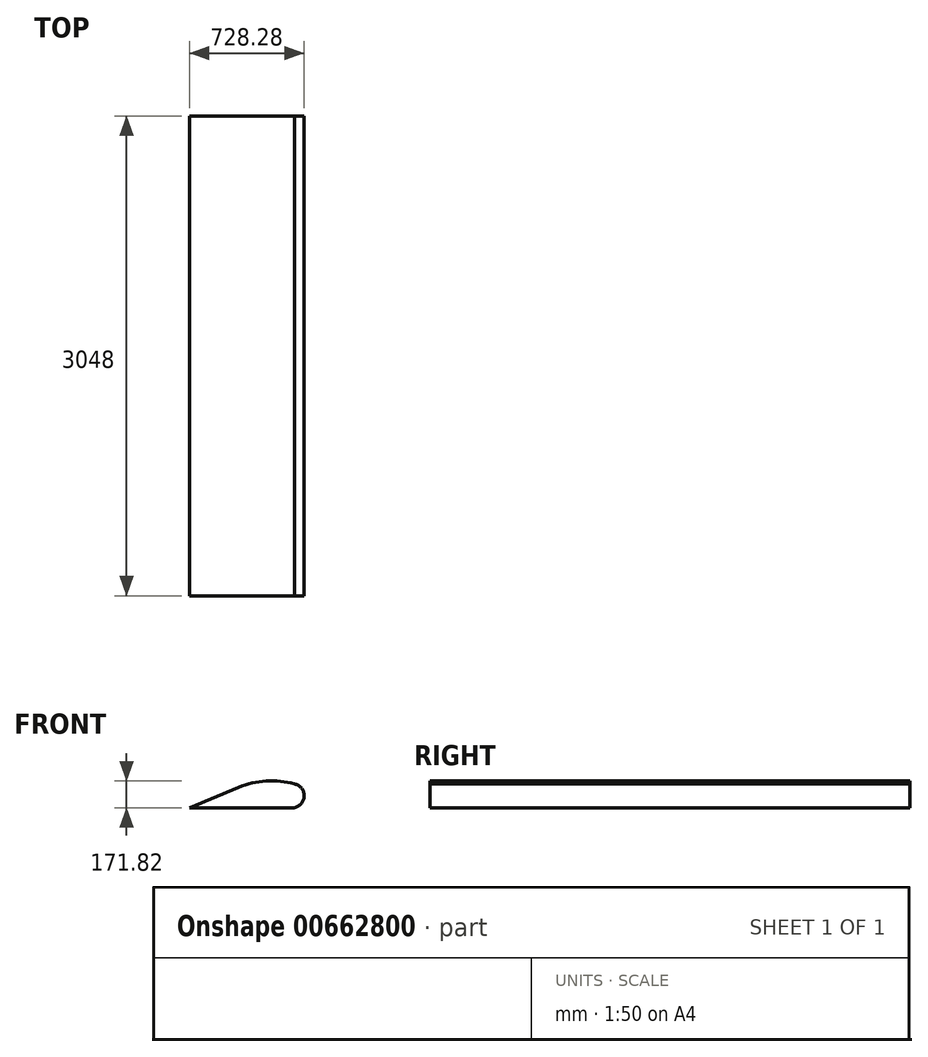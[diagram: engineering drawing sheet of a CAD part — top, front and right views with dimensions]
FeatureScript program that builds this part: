
annotation { "Feature Type Name" : "Feature", "Feature Type Description" : "" }
export const myFeature = defineFeature(function(context is Context, id is Id, definition is map)
    precondition{}
    {
        {
            var Q0;
            Q0=qCreatedBy(makeId("Front.planeOp"),FACE);
            var sketch = newSketch(context, id + "F0", { "sketchPlane" : qUnion([Q0])});
            skArc(sketch, "E0", {"start": v(0, -77.06) * mm, "mid": v(76.64, -7.98) * mm, "end": v(15.88, 75.4) * mm});
            skLineSegment(sketch, "E1", {"start": v(-338.78, 52.8) * mm, "end": v(-651.22, -77.06) * mm});
            skLineSegment(sketch, "E2", {"start": v(-651.22, -77.06) * mm, "end": v(0, -77.06) * mm});
            skArc(sketch, "E3", {"start": v(15.88, 75.4) * mm, "mid": v(-163.34, 93.65) * mm, "end": v(-338.78, 52.8) * mm});
            skSolve(sketch);
        }
        {
            var Q0;
            Q0=makeQuery(id+"F0.imprint","IMPRINT",FACE,{"disambiguationData":[TD([[makeQuery(id+"F0.imprint","IMPRINT",EDGE,{"derivedFrom":sQuery(id+"F0.wireOp",EDGE,"E0")}),1.0]])]});
            extrude(context, id + "F1", {"entities" : qUnion([Q0]), "depth" : 3048 * mm, "offsetDistance" : 25.4 * mm});
        }
    });
